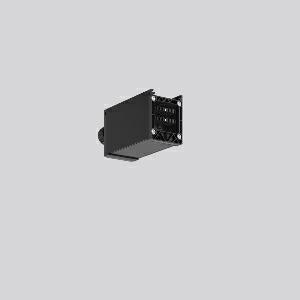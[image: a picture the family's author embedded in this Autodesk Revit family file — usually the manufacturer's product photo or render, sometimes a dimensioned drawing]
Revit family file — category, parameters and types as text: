
# Revit family: linedo_anfangseinspeisung_982859_003_d6cf
name_source: partatom
category: Lighting Fixtures
units: mm (PartAtom-declared; Revit-internal decimal feet)

## family parameters
Cut with Voids When Loaded = No
Host = Face
Light Source = No
Part Type = Normal
Room Calculation Point = No
Round Connector Dimension = Use Diameter
Shared = No

## types (1)
- LINEDO Anfangseinspeisung
    Apparent Load = 0 VA
    Default Elevation = 1800 mm
    Description = Series: LINEDO
Initial power feed (short Version), 7-pole, connection socket. Housing: extruded aluminium profile, powder-coated. Cover made of plastic, surface like housing. LINEDO plug system, plastic, black. 1 cable gland (M25). Cable gland on side or on top. Convenient connection with flat connector.
Colour: black
Length: 134 mm
Width: 58 mm
Height: 76 mm
Weight: 278 g
    Height = 76 mm
    Lamp = 0 x
    Length = 134 mm
    Luminous efficacy = 0 lm/W
    Manufacturer = RZB
    ModVariant = No
    Model = 982859.003
    Mounting Place = Ceiling
    Mounting Type = Surface mounted
    Number of Poles = 1
    OnlyDefault = Yes
    Power Factor = 1
    Product Name = LINEDO Anfangseinspeisung
    Product group = Surface mounted continuous line luminaire system
    ProductGroupID = 310
    Protection Class = Protection class I
    Protection Degree = Degree of protection
    RLX_Detail_Level = 1
    RLX_Emergency_Light_Flux = 0 lm
    RLX_Emergency_Type = 0
    RLX_Emergency_Type_DB = No
    RlxData = <blob elided: 14025 chars, md5=1641efcb>
    Standby Power = 0 W
    System Light Flux = 0 lm
    System Power = 0 W
    Type Comments = Product without accessories
    Type Image = 982859.003.jpg
    URL = http://relux.com
    VarID = ---
    Voltage = 0 V
    Weight = 0.00 kg
    Width = 58 mm

## geometry (parser evidence)
native form markers: Sweep x7
no freeform markers — native parametric forms only
